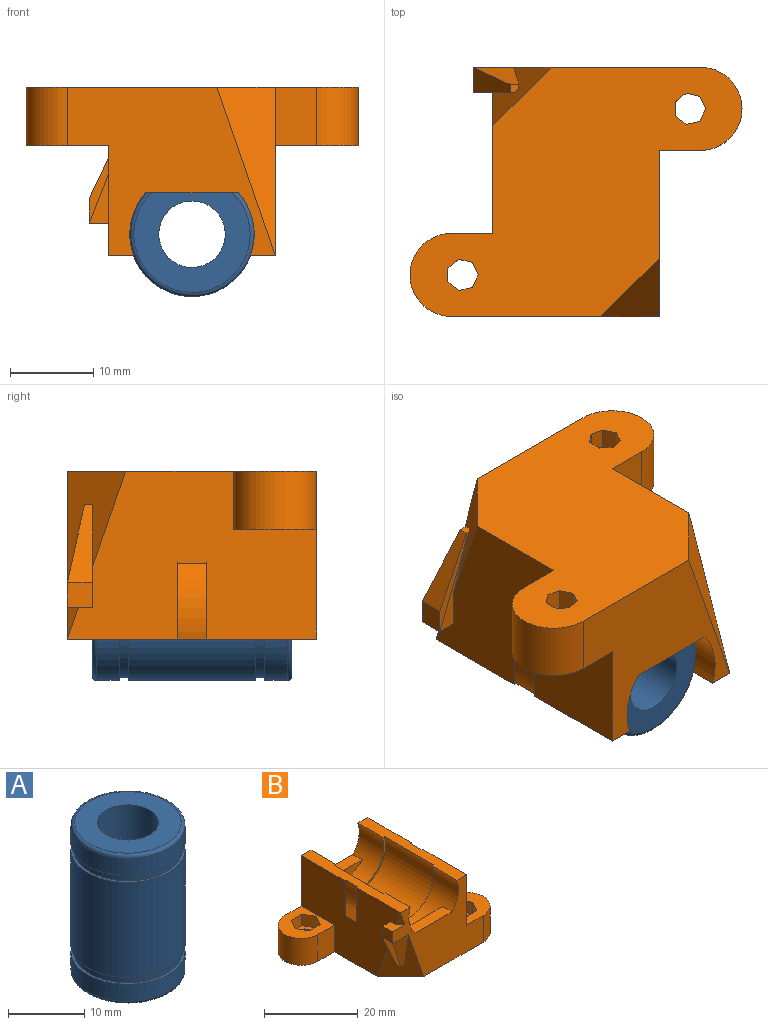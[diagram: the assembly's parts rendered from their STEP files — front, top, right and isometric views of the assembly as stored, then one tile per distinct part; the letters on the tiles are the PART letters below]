
ASSEMBLY  parts=2 mates=1
PART A: 14 faces, bbox 16.2x16.2x24 mm
  f0: plane 15x15mm, normal (0,0,-1), area 16.1mm2, adj f1,f10
  f1: cylinder r=7.15mm len=14.3mm, axis (0,0,-1), area 49.4mm2, adj f0,f2
  f2: plane 15x15mm, normal (0,0,1), area 16.1mm2, adj f1,f3
  f3: cylinder r=7.5mm len=15mm, axis (0,0,-1), area 129.6mm2, adj f2,f12
  f4: plane 14x14mm, normal (0,0,-1), area 103.7mm2, adj f11,f12
  f5: plane 14x14mm, normal (0,0,1), area 103.7mm2, adj f11,f13
  f6: cylinder r=7.5mm len=15mm, axis (0,0,-1), area 129.6mm2, adj f7,f13
  f7: plane 15x15mm, normal (0,0,-1), area 16.1mm2, adj f6,f8
  f8: cylinder r=7.15mm len=14.3mm, axis (0,0,-1), area 49.4mm2, adj f7,f9
  f9: plane 15x15mm, normal (0,0,1), area 16.1mm2, adj f8,f10
  f10: cylinder r=7.5mm len=15.3mm, axis (0,0,-1), area 721mm2, adj f0,f9
  f11: cylinder r=4mm len=24mm, axis (0,0,1), area 603.2mm2, adj f4,f5
  f12: torus R=7mm, axis (0,0,1), area 36.1mm2, adj f3,f4
  f13: torus R=7mm, axis (0,0,-1), area 36.1mm2, adj f5,f6
PART B: 72 faces, bbox 40x30x20.2 mm
  f0: plane 9.37x4.45mm, normal (-0.9,0,-0.43), area 20.7mm2, adj f1,f2,f3,f4
  f1: plane 1x1mm, normal (0,0,-1), area 0.9mm2, adj f0,f2,f5,f6,f7
  f2: plane 9.37x5.45mm, normal (0,-0.98,-0.21), area 28.1mm2, adj f0,f1,f6,f8,f9
  f3: plane 3x3mm, normal (-1,0,0), area 9mm2, adj f0,f4,f8,f10
  f4: plane 12.37x4.45mm, normal (-0.01,1,0), area 8.9mm2, adj f0,f3,f7,f11
  f5: plane 1x0.49mm, normal (1,0,0), area 0.3mm2, adj f1,f6,f9,f12
  f6: plane 13.37x7mm, normal (-0.69,-0.69,-0.24), area 66.7mm2, adj f1,f2,f5,f7,f8,f9,f11,f12
  f7: plane 1x0.49mm, normal (0,1,0), area 0.3mm2, adj f1,f4,f6,f11
  f8: plane 27.38x20.18mm, normal (0,-1,0), area 274.7mm2, adj f2,f3,f6,f10,f13,f14,f15,f16
  f9: plane 7.16x1.58mm, normal (0.97,-0.26,0), area 1.1mm2, adj f2,f5,f6,f12
  f10: plane 3.71x3mm, normal (0,0,1), area 8mm2, adj f3,f8,f11,f14,f15
  f11: plane 11.37x4.59mm, normal (0,1,0.01), area 9mm2, adj f4,f6,f7,f10,f14
  f12: plane 1.22x0.37mm, normal (1,0,0.05), area 0.1mm2, adj f5,f6,f9
  f13: plane 39.98x30mm, normal (0,0,-1), area 708.9mm2, adj f6,f8,f14,f16,f17,f18,f19,f29
  f14: plane 30x20.18mm, normal (-1,0,0), area 428.5mm2, adj f6,f8,f10,f11,f13,f15,f18,f19
  f15: plane 3.8x1.32mm, normal (-0.69,-0.69,-0.24), area 3.6mm2, adj f8,f10,f14
  f16: plane 30x20.18mm, normal (1,0,0), area 432.7mm2, adj f8,f13,f17,f18,f23,f24,f25,f28
  f17: plane 20.17x7mm, normal (0.69,0.69,-0.24), area 102.8mm2, adj f13,f16,f18
  f18: plane 24.99x20.18mm, normal (0,1,0), area 262mm2, adj f13,f14,f16,f17,f20,f21,f28,f33
  f19: plane 7x4.99mm, normal (0,-1,0), area 34.9mm2, adj f13,f14,f20,f34
  f20: plane 10x9.99mm, normal (0,0,1), area 62.6mm2, adj f14,f18,f19,f34,f35,f36,f37,f38
  f21: plane 30x2.93mm, normal (0,0,1), area 78.9mm2, adj f8,f14,f18,f22,f26,f27,f33,f39
  f22: plane 2.51x0.32mm, normal (0,-1,0), area 0.3mm2, adj f14,f21,f42
  f23: plane 20x12mm, normal (0,-1,0), area 51.1mm2, adj f14,f16,f24,f42
  f24: cylinder r=12mm len=20mm, axis (0,1,0), area 82.7mm2, adj f14,f16,f23,f25
  f25: plane 20x12mm, normal (0,1,0), area 51.1mm2, adj f14,f16,f24,f42
  f26: plane 2.51x0.32mm, normal (0,1,0), area 0.3mm2, adj f14,f21,f42
  f27: cylinder r=7.5mm len=15mm, axis (0,-1,0), area 179.7mm2, adj f8,f21,f28,f41,f43,f44
  f28: plane 30x2.93mm, normal (0,0,1), area 78.9mm2, adj f8,f16,f18,f27,f31,f32,f33,f39
  f29: plane 7x4.99mm, normal (0,1,0), area 34.9mm2, adj f13,f16,f30,f45
  f30: plane 10x9.99mm, normal (0,0,1), area 62.6mm2, adj f8,f16,f29,f45,f46,f47,f48,f49
  f31: plane 2.51x0.32mm, normal (0,1,0), area 0.3mm2, adj f16,f28,f42
  f32: plane 2.51x0.32mm, normal (0,-1,0), area 0.3mm2, adj f16,f28,f42
  f33: cylinder r=7.5mm len=15mm, axis (0,-1,0), area 179.7mm2, adj f18,f21,f28,f39,f50,f51
  f34: cylinder r=5mm len=10mm, axis (0,0,-1), area 110mm2, adj f13,f18,f19,f20
  f35: plane 3.2x3mm, normal (0,1,0), area 9.6mm2, adj f20,f36,f52,f54
  f36: plane 3x2.77mm, normal (-0.87,0.5,0), area 9.6mm2, adj f20,f35,f37,f52
  f37: plane 3x2.77mm, normal (-0.87,-0.5,0), area 9.6mm2, adj f20,f36,f38,f52
  f38: plane 3.2x3mm, normal (0,-1,0), area 9.6mm2, adj f20,f37,f52,f53
  f39: plane 16x10.51mm, normal (0,-1,0), area 14.7mm2, adj f21,f28,f33,f40
  f40: cylinder r=8mm len=16mm, axis (0,-1,0), area 453.4mm2, adj f21,f28,f39,f41
  f41: plane 16x10.51mm, normal (0,1,0), area 14.7mm2, adj f21,f27,f28,f40
  f42: cylinder r=10mm len=20mm, axis (0,1,0), area 127.7mm2, adj f21,f22,f23,f25,f26,f28,f31,f32
  f43: plane 11.18x2.8mm, normal (0,0,1), area 31.3mm2, adj f8,f27,f44
  f44: plane 11.18x2.5mm, normal (0,1,0), area 19.4mm2, adj f27,f43
  f45: cylinder r=5mm len=10mm, axis (0,0,-1), area 110mm2, adj f8,f13,f29,f30
  f46: plane 3.2x3mm, normal (0,-1,0), area 9.6mm2, adj f30,f47,f62,f64
  f47: plane 3x2.77mm, normal (0.87,-0.5,0), area 9.6mm2, adj f30,f46,f48,f62
  f48: plane 3x2.77mm, normal (0.87,0.5,0), area 9.6mm2, adj f30,f47,f49,f62
  f49: plane 3.2x3mm, normal (0,1,0), area 9.6mm2, adj f30,f48,f62,f63
  f50: plane 11.18x2.8mm, normal (0,0,1), area 31.3mm2, adj f18,f33,f51
  f51: plane 11.18x2.5mm, normal (0,-1,0), area 19.4mm2, adj f33,f50
  f52: plane 6.4x5.54mm, normal (0,0,1), area 16.4mm2, adj f35,f36,f37,f38,f53,f54,f65,f66
  f53: plane 3x2.77mm, normal (0.87,-0.5,0), area 9.6mm2, adj f20,f38,f52,f54
  f54: plane 3x2.77mm, normal (0.87,0.5,0), area 9.6mm2, adj f20,f35,f52,f53
  f55: plane 4x1.51mm, normal (-0.9,-0.43,0), area 6.7mm2, adj f13,f56,f61,f62
  f56: plane 4x1.63mm, normal (-0.22,-0.97,0), area 6.7mm2, adj f13,f55,f57,f62
  f57: plane 4x1.31mm, normal (0.62,-0.78,0), area 6.7mm2, adj f13,f56,f58,f62
  f58: plane 4x1.68mm, normal (1,0,0), area 6.7mm2, adj f13,f57,f59,f62
  f59: plane 4x1.31mm, normal (0.62,0.78,0), area 6.7mm2, adj f13,f58,f60,f62
  f60: plane 4x1.63mm, normal (-0.22,0.97,0), area 6.7mm2, adj f13,f59,f61,f62
  f61: plane 4x1.51mm, normal (-0.9,0.43,0), area 6.7mm2, adj f13,f55,f60,f62
  f62: plane 6.4x5.54mm, normal (0,0,1), area 16.4mm2, adj f46,f47,f48,f49,f55,f56,f57,f58
  f63: plane 3x2.77mm, normal (-0.87,0.5,0), area 9.6mm2, adj f30,f49,f62,f64
  f64: plane 3x2.77mm, normal (-0.87,-0.5,0), area 9.6mm2, adj f30,f46,f62,f63
  f65: plane 4x1.31mm, normal (0.62,0.78,0), area 6.7mm2, adj f13,f52,f66,f71
  f66: plane 4x1.63mm, normal (-0.22,0.97,0), area 6.7mm2, adj f13,f52,f65,f67
  f67: plane 4x1.51mm, normal (-0.9,0.43,0), area 6.7mm2, adj f13,f52,f66,f68
  f68: plane 4x1.51mm, normal (-0.9,-0.43,0), area 6.7mm2, adj f13,f52,f67,f69
  f69: plane 4x1.63mm, normal (-0.22,-0.97,0), area 6.7mm2, adj f13,f52,f68,f70
  f70: plane 4x1.31mm, normal (0.62,-0.78,0), area 6.7mm2, adj f13,f52,f69,f71
  f71: plane 4x1.68mm, normal (1,0,0), area 6.7mm2, adj f13,f52,f65,f70
PLACE A rot(axis=(-1,0,0),90deg) t=(-88.01,-99.62,-19.17)mm
PLACE B rot(axis=(1,0,0),180deg) t=(-88.01,-87.62,-1.5)mm
MATE fastened A.f1 <-> B.f24  axis (0,-1,0) through (-88.01,-87.62,-19.17)mm
